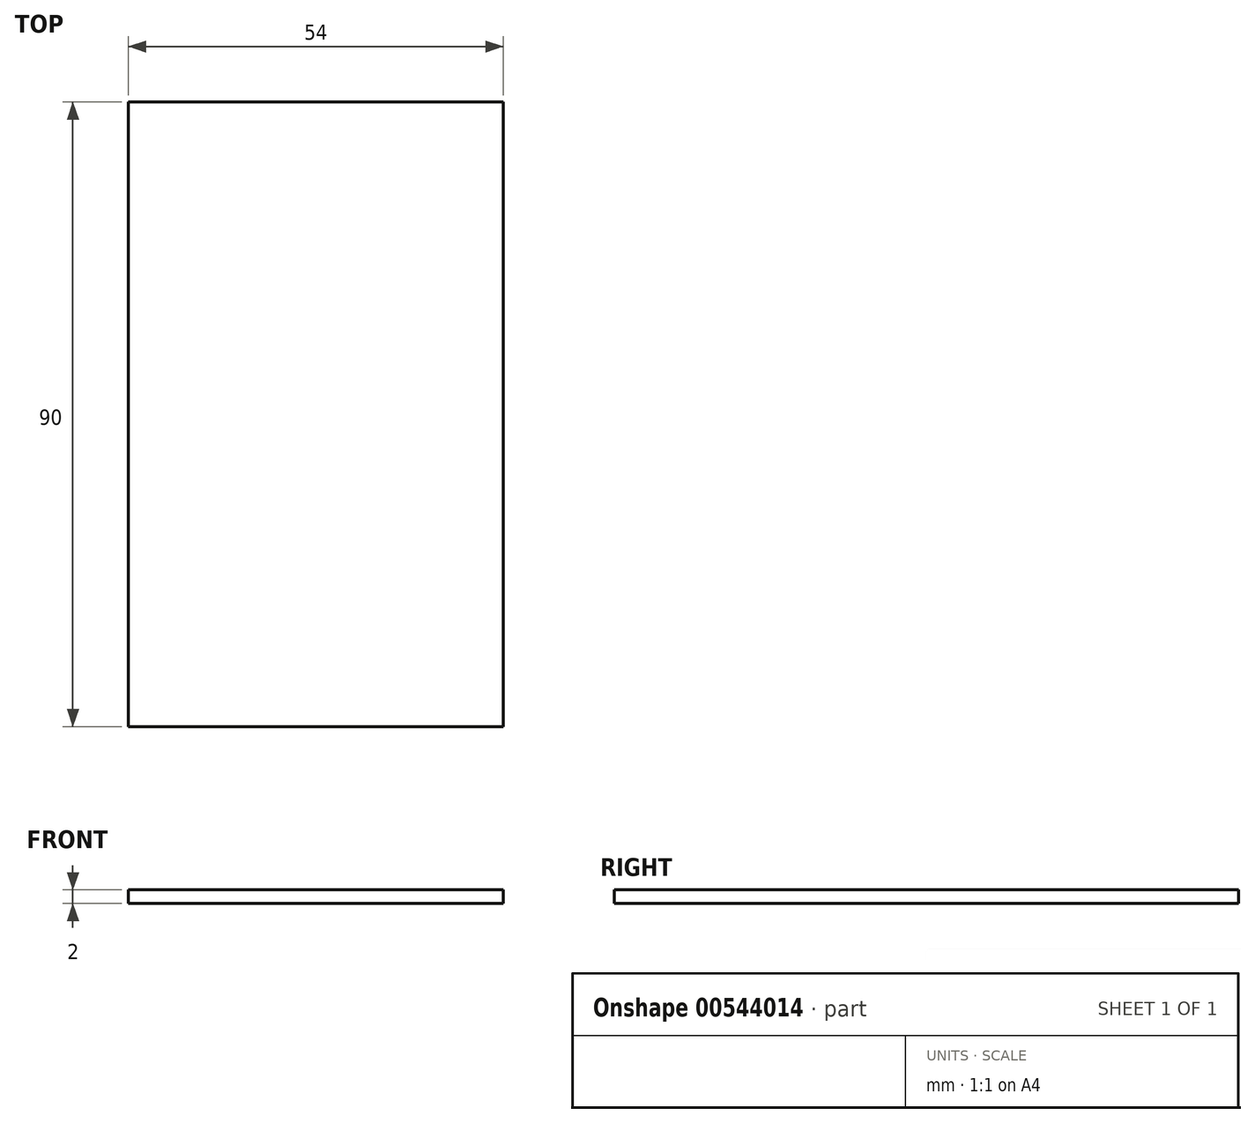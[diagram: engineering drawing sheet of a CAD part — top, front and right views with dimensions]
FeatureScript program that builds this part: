
annotation { "Feature Type Name" : "Feature", "Feature Type Description" : "" }
export const myFeature = defineFeature(function(context is Context, id is Id, definition is map)
    precondition{}
    {
        {
            var Q0;
            Q0=qCreatedBy(makeId("Top.planeOp"),FACE);
            var sketch = newSketch(context, id + "F0", { "sketchPlane" : qUnion([Q0])});
            skLineSegment(sketch, "E0.bottom", {"start": v(27, -45) * mm, "end": v(-27, -45) * mm});
            skLineSegment(sketch, "E0.top", {"start": v(27, 45) * mm, "end": v(-27, 45) * mm});
            skLineSegment(sketch, "E0.left", {"start": v(27, -45) * mm, "end": v(27, 45) * mm});
            skLineSegment(sketch, "E0.right", {"start": v(-27, -45) * mm, "end": v(-27, 45) * mm});
            skPoint(sketch, "E0.middle", {"position": v(0, 0) * mm});
            skSolve(sketch);
        }
        {
            var Q0;
            Q0 = qSketchRegion(id + "F0", true);
            extrude(context, id + "F1", {"entities" : qUnion([Q0]), "depth" : 2 * mm, "offsetDistance" : 25 * mm});
        }
    });
